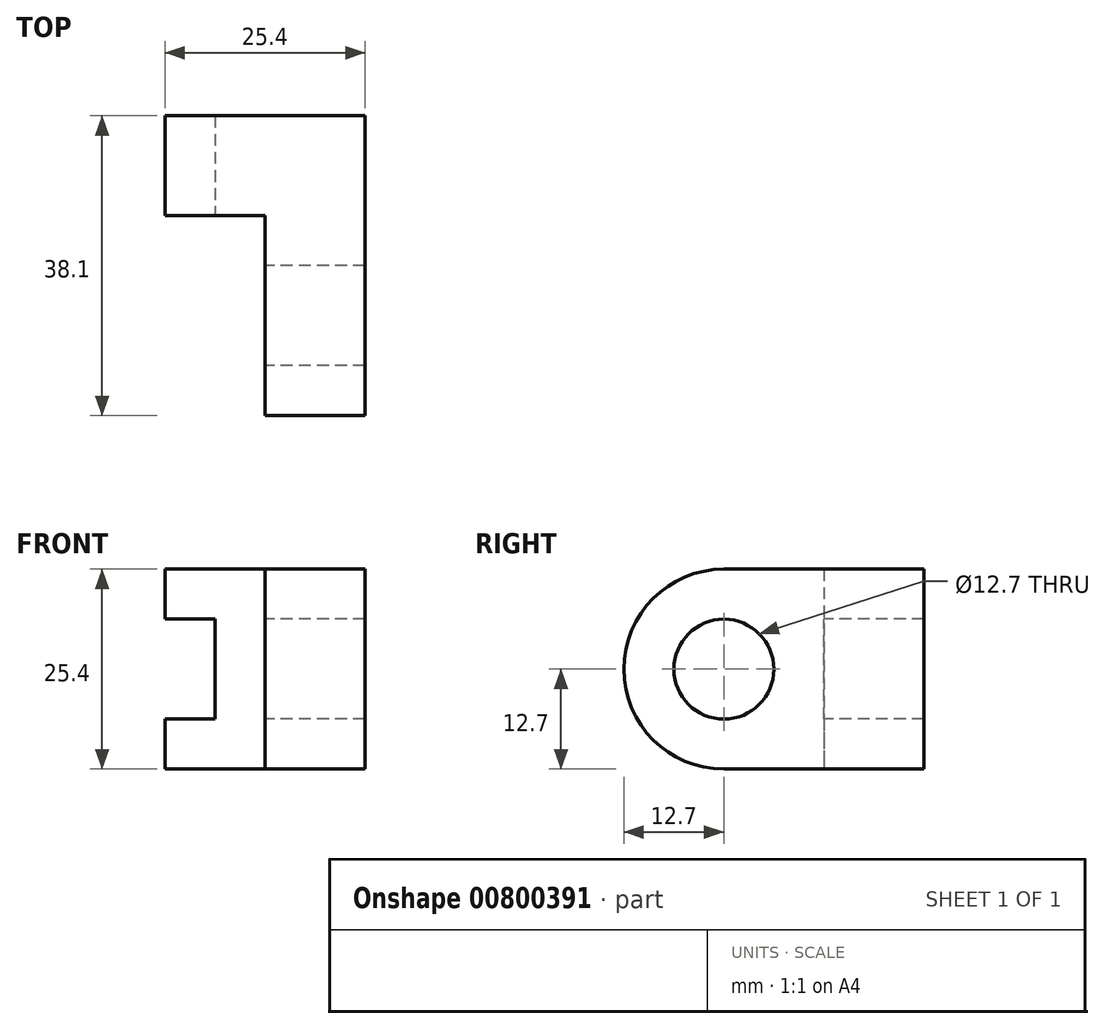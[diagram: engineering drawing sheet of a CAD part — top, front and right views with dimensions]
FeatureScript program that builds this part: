
annotation { "Feature Type Name" : "Feature", "Feature Type Description" : "" }
export const myFeature = defineFeature(function(context is Context, id is Id, definition is map)
    precondition{}
    {
        {
            var Q0;
            Q0=qCreatedBy(makeId("Top.planeOp"),FACE);
            var sketch = newSketch(context, id + "F0", { "sketchPlane" : qUnion([Q0])});
            skLineSegment(sketch, "E0", {"start": v(0, 0) * mm, "end": v(0, -12.7) * mm});
            skLineSegment(sketch, "E1", {"start": v(0, 0) * mm, "end": v(25.4, 0) * mm});
            skLineSegment(sketch, "E2", {"start": v(25.4, 0) * mm, "end": v(25.4, -50.8) * mm});
            skLineSegment(sketch, "E3", {"start": v(25.4, -50.8) * mm, "end": v(12.7, -50.8) * mm});
            skLineSegment(sketch, "E4", {"start": v(12.7, -50.8) * mm, "end": v(12.7, -12.7) * mm});
            skLineSegment(sketch, "E5", {"start": v(12.7, -12.7) * mm, "end": v(0, -12.7) * mm});
            skSolve(sketch);
        }
        {
            var Q0;
            Q0 = qSketchRegion(id + "F0", true);
            extrude(context, id + "F1", {"entities" : qUnion([Q0]), "depth" : 25.4 * mm, "offsetDistance" : 25.4 * mm});
        }
        {
            var Q0;
            Q0=makeQuery(id+"F1.opExtrude","SWEPT_FACE",FACE,{"disambiguationData":[OSD([sQuery(id+"F0.wireOp",EDGE,"E5")])]});
            var sketch = newSketch(context, id + "F2", { "sketchPlane" : qUnion([Q0])});
            skLineSegment(sketch, "E6", {"start": v(0, 25.4) * mm, "end": v(12.7, 25.4) * mm});
            skLineSegment(sketch, "E7", {"start": v(12.7, 25.4) * mm, "end": v(12.7, 0) * mm});
            skLineSegment(sketch, "E8", {"start": v(12.7, 0) * mm, "end": v(0, 0) * mm});
            skLineSegment(sketch, "E9", {"start": v(0, 0) * mm, "end": v(0, 6.35) * mm});
            skLineSegment(sketch, "E10", {"start": v(0, 25.4) * mm, "end": v(0, 19.05) * mm});
            skLineSegment(sketch, "E11", {"start": v(0, 19.05) * mm, "end": v(6.35, 19.05) * mm});
            skLineSegment(sketch, "E12", {"start": v(0, 6.35) * mm, "end": v(6.35, 6.35) * mm});
            skLineSegment(sketch, "E13", {"start": v(6.35, 6.35) * mm, "end": v(6.35, 19.05) * mm});
            skSolve(sketch);
        }
        {
            var Q0;
            {var subQ0=sQuery(id+"F2.wireOp",EDGE,"E11");Q0=makeQuery(id+"F2.imprint","IMPRINT",FACE,{"disambiguationData":[TD([[makeQuery(id+"F2.imprint","IMPRINT",EDGE,{"derivedFrom":subQ0}),-1.0]])]});}
            extrude(context, id + "F3", {"entities" : qUnion([Q0]), "operationType" : NewBodyOperationType.REMOVE, "endBound" : BoundingType.THROUGH_ALL, "oppositeDirection" : true, "depth" : 25.4 * mm, "offsetDistance" : 25.4 * mm});
        }
        {
            var Q0;
            Q0=makeQuery(id+"F1.opExtrude","SWEPT_FACE",FACE,{"disambiguationData":[OSD([sQuery(id+"F0.wireOp",EDGE,"E4")])]});
            var sketch = newSketch(context, id + "F4", { "sketchPlane" : qUnion([Q0])});
            skLineSegment(sketch, "E14", {"start": v(12.7, 12.7) * mm, "end": v(25.4, 12.7) * mm, "construction": true});
            skCircle(sketch, "E15", {"center": v(25.4, 12.7) * mm, "radius": 6.35 * mm});
            skSolve(sketch);
        }
        {
            var Q0;
            Q0=makeQuery(id+"F4.imprint","IMPRINT",FACE,{"disambiguationData":[TD([[makeQuery(id+"F4.imprint","IMPRINT",EDGE,{"derivedFrom":sQuery(id+"F4.wireOp",EDGE,"E15")}),1.0]])]});
            extrude(context, id + "F5", {"entities" : qUnion([Q0]), "operationType" : NewBodyOperationType.REMOVE, "endBound" : BoundingType.THROUGH_ALL, "oppositeDirection" : true, "depth" : 25.4 * mm, "offsetDistance" : 25.4 * mm});
        }
        {
            var Q0;
            Q0=makeQuery(id+"F1.opExtrude","SWEPT_FACE",FACE,{"disambiguationData":[OSD([sQuery(id+"F0.wireOp",EDGE,"E4")])]});
            var sketch = newSketch(context, id + "F6", { "sketchPlane" : qUnion([Q0])});
            skLineSegment(sketch, "E16", {"start": v(12.7, 25.4) * mm, "end": v(25.4, 25.4) * mm});
            skLineSegment(sketch, "E17", {"start": v(12.7, 0) * mm, "end": v(25.4, 0) * mm});
            skArc(sketch, "E18", {"start": v(25.4, 0) * mm, "mid": v(38.1, 12.7) * mm, "end": v(25.4, 25.4) * mm});
            skSolve(sketch);
        }
        {
            var Q0;
            {var subQ0=sQuery(id+"F6.wireOp",EDGE,"E18");Q0=makeQuery(id+"F6.imprint","IMPRINT",FACE,{"disambiguationData":[TD([[makeQuery(id+"F6.imprint","IMPRINT",EDGE,{"derivedFrom":subQ0}),-1.0]])]});}
            extrude(context, id + "F7", {"entities" : qUnion([Q0]), "operationType" : NewBodyOperationType.ADD, "endBound" : BoundingType.THROUGH_ALL, "depth" : 25.4 * mm, "offsetDistance" : 25.4 * mm});
        }
        {
            var Q0;
            Q0=makeQuery(id+"F7.opExtrude","CAP_FACE",FACE,{"disambiguationData":[OSD([sQuery(id+"F0.wireOp",EDGE,"E3"),sQuery(id+"F0.wireOp",EDGE,"E4"),sQuery(id+"F6.wireOp",EDGE,"E18")])],"isStart":false});
            extrude(context, id + "F8", {"entities" : qUnion([Q0]), "operationType" : NewBodyOperationType.REMOVE, "endBound" : BoundingType.THROUGH_ALL, "oppositeDirection" : true, "depth" : 25.4 * mm, "offsetDistance" : 25.4 * mm});
        }
    });
